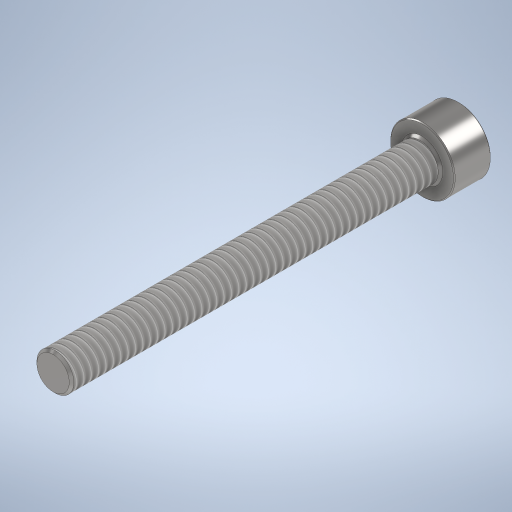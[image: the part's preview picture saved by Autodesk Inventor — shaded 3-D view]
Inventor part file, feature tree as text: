
AUTODESK INVENTOR PART (.ipt)
format: ipt  version: 2024 (Build 280153000, 153)  size: 323,072 bytes
history: native  units: mm
features: extrude x3, chamfer x3, sketch x2, thread x1, hole x1
ambient origin geometry x8: Origin, YZ Plane, XZ Plane, XY Plane, X Axis, Y Axis, Z Axis, Center Point
bodies: Solid1 (feature_tree)
feature tree (10):
  sketch  "Sketch1"  dims[d0=7.0mm d1=4.0mm]
  extrude  "Extrusion1"  Depth=4.0mm
  extrude  "Extrusion2"  Depth=2.0mm TaperAngle=0.0deg
  thread  "Thread1"  [1 undecoded]
  chamfer  "Chamfer1"  Distance=2.0mm Angle=45.0deg
  sketch  "Sketch2"  dims[d2=40.0mm d3=0.0mm d4=4.0mm d5=0.0mm d6=15.0mm d7=0.0mm d8=0.1mm d9=2.0mm d10=45.0deg d11=2.75mm d12=3.0mm d15=0.4mm d16=2.0mm d17=45.0deg d18=3.0mm d19=0.0mm d20=0.25mm d21=2.0mm d22=45.0deg d23=2.75mm d24=6.0mm d25=4.0mm d26=2.0mm d27=90.0deg d28=2.0mm d29=150.0deg]
  hole  "Hole1"  [1 undecoded]
  chamfer  "Chamfer2"  Distance=3.0mm
  extrude  "Extrusion4"  Depth=2.0mm TaperAngle=45.0deg
  chamfer  "Chamfer3"  Distance=3.0mm
note: 2 required parameter values undecoded (feature->parameter linkage not recoverable at this tier; creation-order binding heuristic only, values carry confidence <= 0.55)
